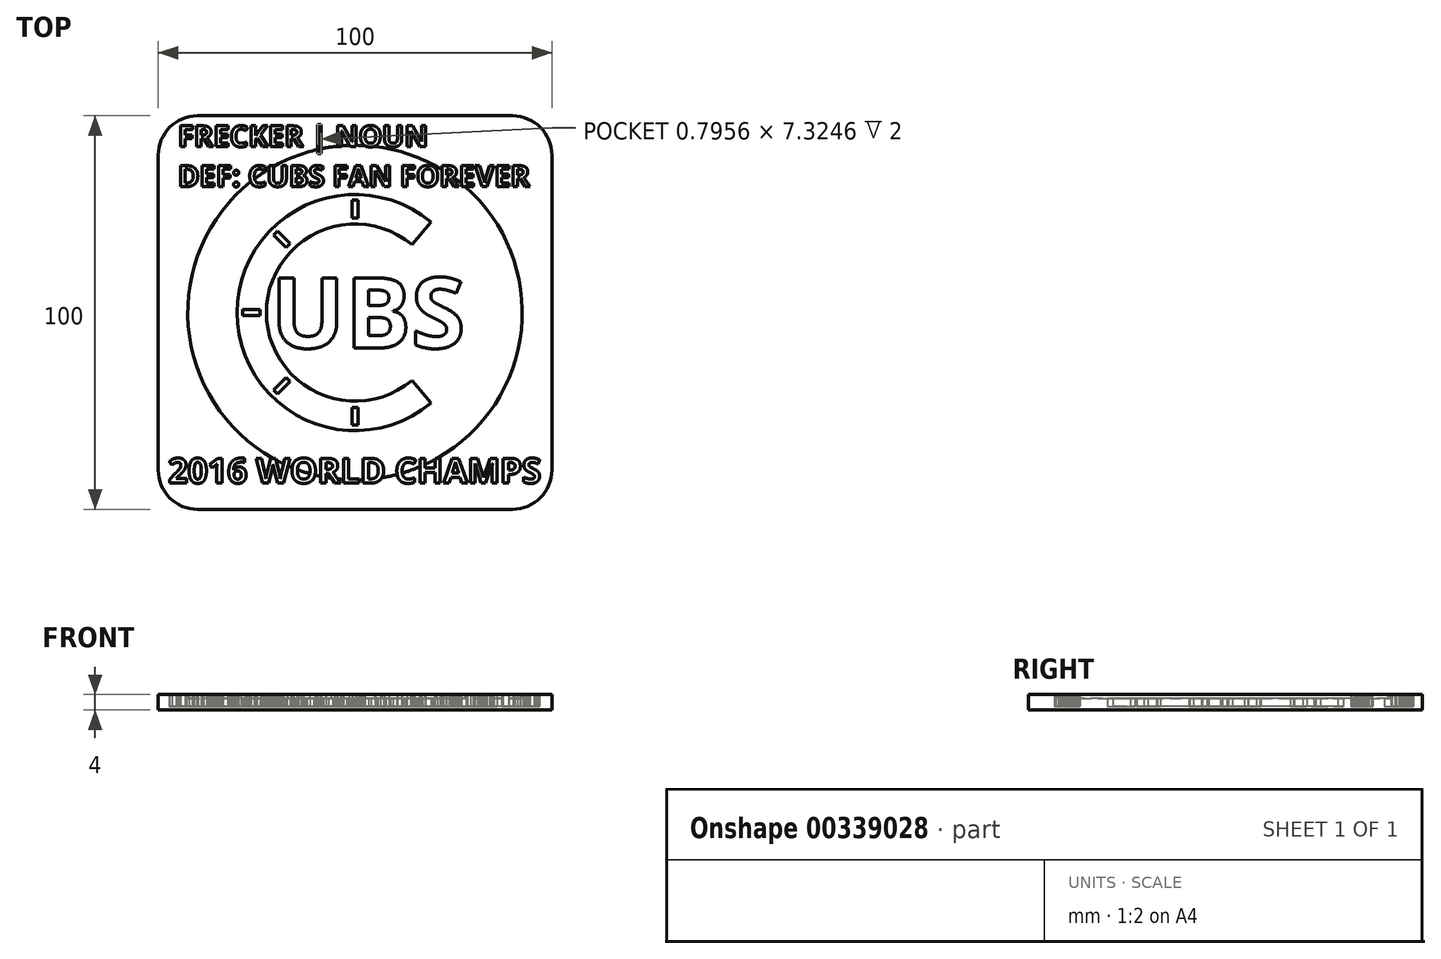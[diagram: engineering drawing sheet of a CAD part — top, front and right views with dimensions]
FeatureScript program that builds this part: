
annotation { "Feature Type Name" : "Feature", "Feature Type Description" : "" }
export const myFeature = defineFeature(function(context is Context, id is Id, definition is map)
    precondition{}
    {
        {
            var Q0;
            Q0=qCreatedBy(makeId("Top.planeOp"),FACE);
            var sketch = newSketch(context, id + "F0", { "sketchPlane" : qUnion([Q0])});
            skLineSegment(sketch, "E0.bottom", {"start": v(-50, 50) * mm, "end": v(50, 50) * mm});
            skLineSegment(sketch, "E0.top", {"start": v(-50, -50) * mm, "end": v(50, -50) * mm});
            skLineSegment(sketch, "E0.left", {"start": v(-50, 50) * mm, "end": v(-50, -50) * mm});
            skLineSegment(sketch, "E0.right", {"start": v(50, 50) * mm, "end": v(50, -50) * mm});
            skSolve(sketch);
        }
        {
            var Q0;
            Q0=makeQuery(id+"F0.imprint","IMPRINT",FACE,{"disambiguationData":[TD([[makeQuery(id+"F0.imprint","IMPRINT",EDGE,{"derivedFrom":sQuery(id+"F0.wireOp",EDGE,"E0.bottom")}),-1.0]])]});
            extrude(context, id + "F1", {"entities" : qUnion([Q0]), "endBound" : BoundingType.SYMMETRIC, "depth" : 4 * mm});
        }
        {
            var Q0;
            Q0=qCreatedBy(makeId("Top.planeOp"),FACE);
            cPlane(context, id + "F2", {"entities" : qUnion([Q0]), "cplaneType" : CPlaneType.OFFSET, "offset" : 1 * mm, "oppositeDirection" : true, "width" : 150 * mm, "height" : 150 * mm});
        }
        {
            var Q0;
            Q0=qCreatedBy(id+"F2.planeOp",FACE);
            var sketch = newSketch(context, id + "F3", { "sketchPlane" : qUnion([Q0])});
            skArc(sketch, "E1", {"start": v(19.28, 22.98) * mm, "mid": v(-30, 0) * mm, "end": v(19.28, -22.98) * mm});
            skArc(sketch, "E2", {"start": v(14.46, 17.24) * mm, "mid": v(-22.5, 0) * mm, "end": v(14.46, -17.24) * mm});
            skText(sketch, "E3", { "text": "UBS", "fontName": "OpenSans-Bold.ttf"});
            skLineSegment(sketch, "E4", {"start": v(14.46, 17.24) * mm, "end": v(19.28, 22.98) * mm});
            skLineSegment(sketch, "E5", {"start": v(14.46, -17.24) * mm, "end": v(19.28, -22.98) * mm});
            skText(sketch, "E6", { "text": "FRECKER | NOUN\nDEF: CUBS FAN FOREVER", "fontName": "OpenSans-Bold.ttf"});
            skText(sketch, "E7", { "text": "2016 WORLD CHAMPS", "fontName": "OpenSans-Bold.ttf"});
            const initialGuessF3  = {"E3": [-0.02138, -0.00898, 1, 0, 0.01796], "E6": [-0.045, 0.04214, 1, 0, 0.00536], "E7": [-0.0475, -0.04333, 1, 0, 0.00635]};
            skSetInitialGuess(sketch, initialGuessF3);
            skSolve(sketch);
        }
        {
            var Q0;
            Q0=qSketchRegion(id+"F3",true);
            extrude(context, id + "F4", {"entities" : qUnion([Q0]), "operationType" : NewBodyOperationType.REMOVE, "oppositeDirection" : true, "depth" : -5 * mm});
        }
        {
            var Q0;
            Q0=makeQuery(id+"F1.opExtrude","CAP_FACE",FACE,{"disambiguationData":[OSD([sQuery(id+"F0.wireOp",EDGE,"E0.bottom"),sQuery(id+"F0.wireOp",EDGE,"E0.top"),sQuery(id+"F0.wireOp",EDGE,"E0.left"),sQuery(id+"F0.wireOp",EDGE,"E0.right")])],"isStart":false});
            var sketch = newSketch(context, id + "F5", { "sketchPlane" : qUnion([Q0])});
            skSolve(sketch);
        }
        {
            var Q0;
            Q0=makeQuery(id+"F5.imprint","IMPRINT",FACE,{"disambiguationData":[TD([[makeQuery(id+"F5.imprint","IMPRINT",EDGE,{"derivedFrom":makeQuery(id+"F1.opExtrude","CAP_EDGE",EDGE,{"disambiguationData":[OSD([sQuery(id+"F0.wireOp",EDGE,"E0.bottom")])],"isStart":false})}),-1.0]])]});
            var sketch = newSketch(context, id + "F6", { "sketchPlane" : qUnion([Q0])});
            skCircle(sketch, "E8", {"center": v(0, 0) * mm, "radius": 42.5 * mm});
            skSolve(sketch);
        }
        {
            var Q0;
            Q0=qSketchRegion(id+"F6",true);
            extrude(context, id + "F7", {"entities" : qUnion([Q0]), "operationType" : NewBodyOperationType.REMOVE, "oppositeDirection" : true, "depth" : 1 * mm});
        }
        {
            var Q0;
            Q0=makeQuery(id+"F1.opExtrude","SWEPT_EDGE",EDGE,{"disambiguationData":[OSD([sQuery(id+"F0.wireOp",EDGE,"E0.top"),sQuery(id+"F0.wireOp",EDGE,"E0.left")])]});
            var Q1;
            Q1=makeQuery(id+"F1.opExtrude","SWEPT_EDGE",EDGE,{"disambiguationData":[OSD([sQuery(id+"F0.wireOp",EDGE,"E0.bottom"),sQuery(id+"F0.wireOp",EDGE,"E0.left")])]});
            var Q2;
            Q2=makeQuery(id+"F1.opExtrude","SWEPT_EDGE",EDGE,{"disambiguationData":[OSD([sQuery(id+"F0.wireOp",EDGE,"E0.bottom"),sQuery(id+"F0.wireOp",EDGE,"E0.right")])]});
            var Q3;
            Q3=makeQuery(id+"F1.opExtrude","SWEPT_EDGE",EDGE,{"disambiguationData":[OSD([sQuery(id+"F0.wireOp",EDGE,"E0.top"),sQuery(id+"F0.wireOp",EDGE,"E0.right")])]});
            fillet(context, id + "F8", {"entities" : qUnion([Q0, Q1, Q2, Q3]), "radius" : 10 * mm, "tangentPropagation" : true, "allowEdgeOverflow" : false});
        }
        {
            var Q0;
            Q0=makeQuery(id+"F4.boolean.opBoolean","COPY",FACE,{"derivedFrom":makeQuery(id+"F4.opExtrude","CAP_FACE",FACE,{"disambiguationData":[OSD([sQuery(id+"F3.wireOp",EDGE,"E1"),sQuery(id+"F3.wireOp",EDGE,"E2"),sQuery(id+"F3.wireOp",EDGE,"E4"),sQuery(id+"F3.wireOp",EDGE,"E5")])],"isStart":true})});
            var sketch = newSketch(context, id + "F9", { "sketchPlane" : qUnion([Q0])});
            skLineSegment(sketch, "E9", {"start": v(-0.75, 28.57) * mm, "end": v(-0.75, 24.07) * mm});
            skLineSegment(sketch, "E10", {"start": v(-0.75, 24.07) * mm, "end": v(0.75, 24.07) * mm});
            skLineSegment(sketch, "E11", {"start": v(0.75, 24.07) * mm, "end": v(0.75, 28.57) * mm});
            skLineSegment(sketch, "E12", {"start": v(0.75, 28.57) * mm, "end": v(-0.75, 28.57) * mm});
            skLineSegment(sketch, "E13.1.0", {"start": v(-17.55, 16.5) * mm, "end": v(-16.5, 17.55) * mm});
            skLineSegment(sketch, "E13.1.1", {"start": v(-20.73, 19.67) * mm, "end": v(-17.55, 16.5) * mm});
            skLineSegment(sketch, "E13.1.2", {"start": v(-16.5, 17.55) * mm, "end": v(-19.67, 20.73) * mm});
            skLineSegment(sketch, "E13.1.3", {"start": v(-19.67, 20.73) * mm, "end": v(-20.73, 19.67) * mm});
            skLineSegment(sketch, "E13.2.0", {"start": v(-24.07, -0.75) * mm, "end": v(-24.07, 0.75) * mm});
            skLineSegment(sketch, "E13.2.1", {"start": v(-28.57, -0.75) * mm, "end": v(-24.07, -0.75) * mm});
            skLineSegment(sketch, "E13.2.2", {"start": v(-24.07, 0.75) * mm, "end": v(-28.57, 0.75) * mm});
            skLineSegment(sketch, "E13.2.3", {"start": v(-28.57, 0.75) * mm, "end": v(-28.57, -0.75) * mm});
            skLineSegment(sketch, "E13.3.0", {"start": v(-16.5, -17.55) * mm, "end": v(-17.55, -16.5) * mm});
            skLineSegment(sketch, "E13.3.1", {"start": v(-19.67, -20.73) * mm, "end": v(-16.5, -17.55) * mm});
            skLineSegment(sketch, "E13.3.2", {"start": v(-17.55, -16.5) * mm, "end": v(-20.73, -19.67) * mm});
            skLineSegment(sketch, "E13.3.3", {"start": v(-20.73, -19.67) * mm, "end": v(-19.67, -20.73) * mm});
            skLineSegment(sketch, "E13.4.0", {"start": v(0.75, -24.07) * mm, "end": v(-0.75, -24.07) * mm});
            skLineSegment(sketch, "E13.4.1", {"start": v(0.75, -28.57) * mm, "end": v(0.75, -24.07) * mm});
            skLineSegment(sketch, "E13.4.2", {"start": v(-0.75, -24.07) * mm, "end": v(-0.75, -28.57) * mm});
            skLineSegment(sketch, "E13.4.3", {"start": v(-0.75, -28.57) * mm, "end": v(0.75, -28.57) * mm});
            skPoint(sketch, "E13.center", {"position": v(0, 0) * mm});
            skSolve(sketch);
        }
        {
            var Q0;
            Q0 = qSketchRegion(id + "F9", true);
            extrude(context, id + "F10", {"entities" : qUnion([Q0]), "operationType" : NewBodyOperationType.ADD, "depth" : 2 * mm});
        }
    });
